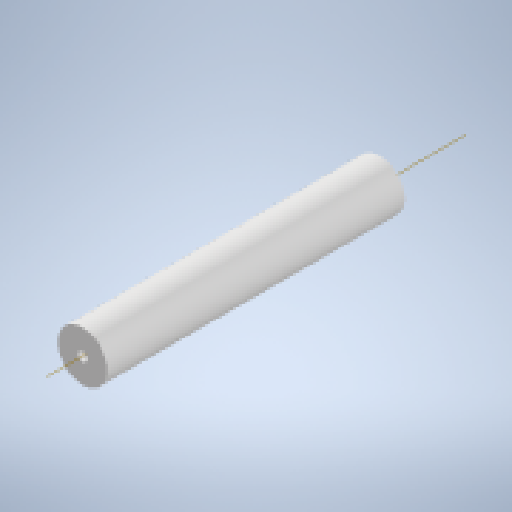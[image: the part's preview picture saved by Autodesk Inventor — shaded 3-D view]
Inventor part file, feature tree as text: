
AUTODESK INVENTOR PART (.ipt)
format: ipt  version: 2023 (Build 270158000, 158)  size: 229,376 bytes
history: native  units: mm
features: other x2, extrude x1, sketch x1
ambient origin geometry x8: Origin, YZ Plane, XZ Plane, XY Plane, X Axis, Y Axis, Z Axis, Center Point
bodies: Solid1 (feature_tree)
feature tree (4):
  other  "roller"
  extrude  "Extrusion1"  Depth=10.0mm
  other  "Work Axis1"
  sketch  "Sketch1"  dims[d0=50.0mm d1=10.0mm d2=300.0mm d3=0.0mm]
